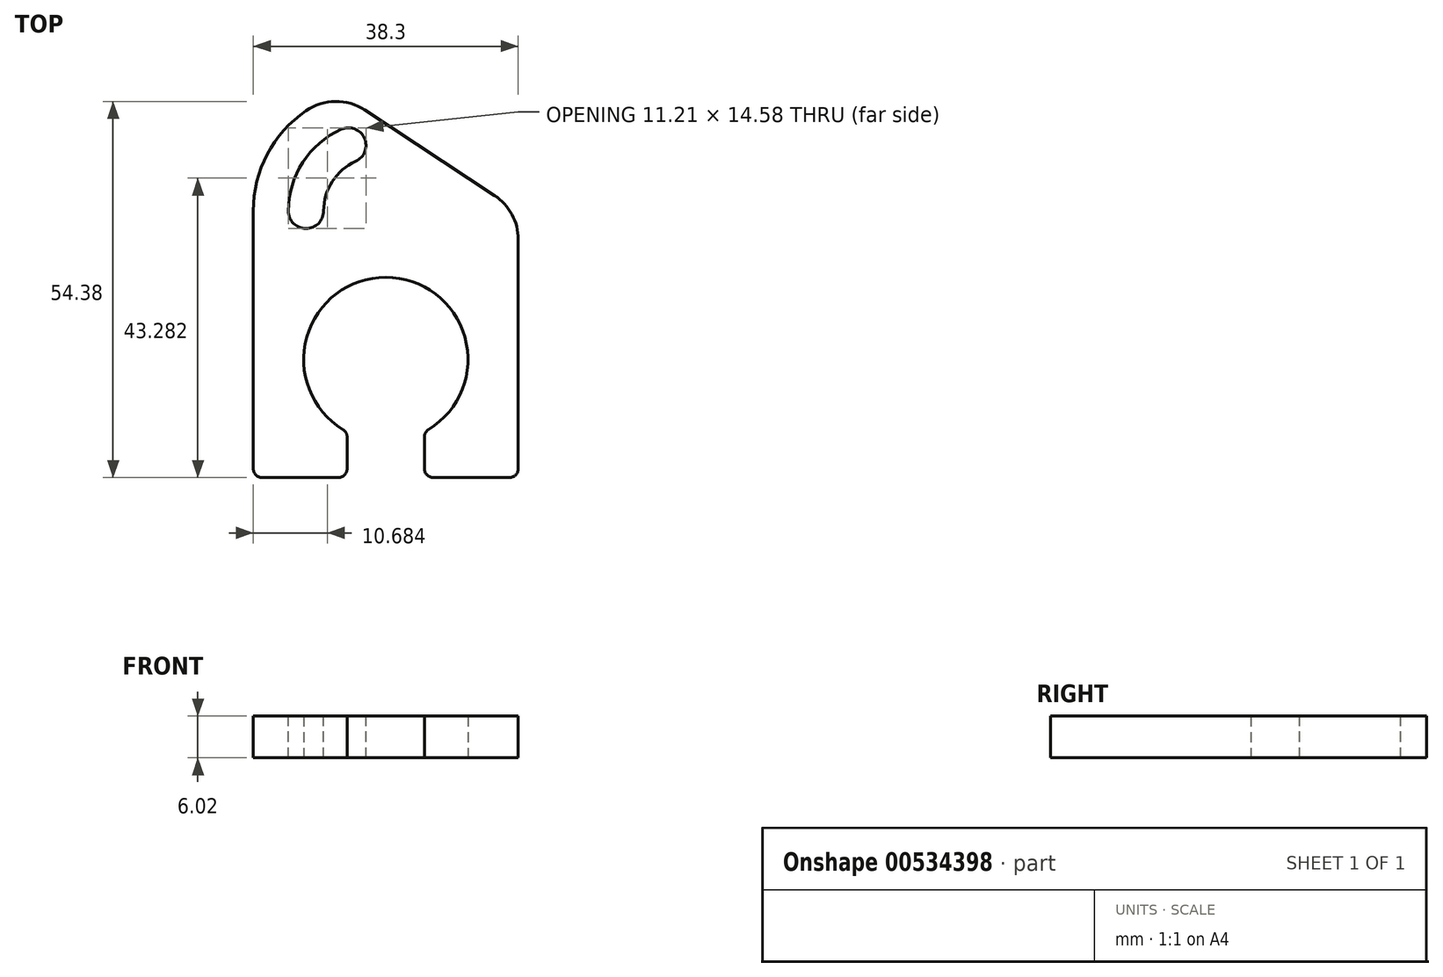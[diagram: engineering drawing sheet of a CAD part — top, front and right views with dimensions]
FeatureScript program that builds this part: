
annotation { "Feature Type Name" : "Feature", "Feature Type Description" : "" }
export const myFeature = defineFeature(function(context is Context, id is Id, definition is map)
    precondition{}
    {
        {
            var Q0;
            Q0=qCreatedBy(makeId("Top.planeOp"),FACE);
            var sketch = newSketch(context, id + "F0", { "sketchPlane" : qUnion([Q0])});
            skArc(sketch, "E0", {"start": v(5.59, -10.48) * mm, "mid": v(0, 11.87) * mm, "end": v(-5.59, -10.48) * mm});
            skLineSegment(sketch, "E1", {"start": v(19.15, -17.08) * mm, "end": v(19.15, 21.45) * mm});
            skLineSegment(sketch, "E2", {"start": v(19.15, 21.45) * mm, "end": v(-6.5, 38.34) * mm});
            skLineSegment(sketch, "E3", {"start": v(-19.15, -17.08) * mm, "end": v(-19.15, 21.45) * mm});
            skLineSegment(sketch, "E4", {"start": v(-19.15, -17.08) * mm, "end": v(-5.59, -17.08) * mm});
            skLineSegment(sketch, "E5", {"start": v(5.59, -17.08) * mm, "end": v(19.15, -17.08) * mm});
            skLineSegment(sketch, "E6", {"start": v(-5.59, -10.48) * mm, "end": v(-5.59, -17.08) * mm});
            skLineSegment(sketch, "E7", {"start": v(5.59, -10.48) * mm, "end": v(5.59, -17.08) * mm});
            skArc(sketch, "E8", {"start": v(-19.15, 21.45) * mm, "mid": v(-15.64, 32) * mm, "end": v(-6.5, 38.34) * mm});
            skSolve(sketch);
        }
        {
            var Q0;
            Q0=makeQuery(id+"F0.imprint","IMPRINT",FACE,{"disambiguationData":[TD([[makeQuery(id+"F0.imprint","IMPRINT",EDGE,{"derivedFrom":sQuery(id+"F0.wireOp",EDGE,"E0")}),-1.0]])]});
            extrude(context, id + "F1", {"entities" : qUnion([Q0]), "depth" : 6.02 * mm, "offsetDistance" : 25.4 * mm});
        }
        {
            var Q0;
            Q0=makeQuery(id+"F1.opExtrude","CAP_FACE",FACE,{"disambiguationData":[OSD([sQuery(id+"F0.wireOp",EDGE,"E0"),sQuery(id+"F0.wireOp",EDGE,"E1"),sQuery(id+"F0.wireOp",EDGE,"E2"),sQuery(id+"F0.wireOp",EDGE,"E3"),sQuery(id+"F0.wireOp",EDGE,"E4"),sQuery(id+"F0.wireOp",EDGE,"E5"),sQuery(id+"F0.wireOp",EDGE,"E6"),sQuery(id+"F0.wireOp",EDGE,"E7"),sQuery(id+"F0.wireOp",EDGE,"E8")])],"isStart":false});
            var sketch = newSketch(context, id + "F2", { "sketchPlane" : qUnion([Q0])});
            skArc(sketch, "E9", {"start": v(-14.07, 21.45) * mm, "mid": v(-11.53, 18.91) * mm, "end": v(-9, 21.45) * mm});
            skArc(sketch, "E10", {"start": v(-14.07, 21.45) * mm, "mid": v(-12, 28.48) * mm, "end": v(-6.44, 33.27) * mm});
            skArc(sketch, "E11", {"start": v(-9, 21.45) * mm, "mid": v(-7.73, 25.73) * mm, "end": v(-4.35, 28.64) * mm});
            skArc(sketch, "E12", {"start": v(-4.35, 28.64) * mm, "mid": v(-3.08, 32) * mm, "end": v(-6.44, 33.27) * mm});
            skSolve(sketch);
        }
        {
            var Q0;
            Q0=makeQuery(id+"F2.imprint","IMPRINT",FACE,{"disambiguationData":[TD([[makeQuery(id+"F2.imprint","IMPRINT",EDGE,{"derivedFrom":sQuery(id+"F2.wireOp",EDGE,"E9")}),1.0]])]});
            var Q1;
            Q1=makeQuery(id+"F1.opExtrude","CAP_FACE",FACE,{"disambiguationData":[OSD([sQuery(id+"F0.wireOp",EDGE,"E0"),sQuery(id+"F0.wireOp",EDGE,"E1"),sQuery(id+"F0.wireOp",EDGE,"E2"),sQuery(id+"F0.wireOp",EDGE,"E3"),sQuery(id+"F0.wireOp",EDGE,"E4"),sQuery(id+"F0.wireOp",EDGE,"E5"),sQuery(id+"F0.wireOp",EDGE,"E6"),sQuery(id+"F0.wireOp",EDGE,"E7"),sQuery(id+"F0.wireOp",EDGE,"E8")])],"isStart":true});
            extrude(context, id + "F3", {"entities" : qUnion([Q0]), "operationType" : NewBodyOperationType.REMOVE, "endBound" : BoundingType.UP_TO_SURFACE, "oppositeDirection" : true, "depth" : 25.4 * mm, "endBoundEntityFace" : qUnion([Q1]), "offsetDistance" : 25.4 * mm});
        }
        {
            var Q0;
            Q0=makeQuery(id+"F1.opExtrude","SWEPT_EDGE",EDGE,{"disambiguationData":[OSD([sQuery(id+"F0.wireOp",EDGE,"E2"),sQuery(id+"F0.wireOp",EDGE,"E8")])]});
            var Q1;
            Q1=makeQuery(id+"F1.opExtrude","SWEPT_EDGE",EDGE,{"disambiguationData":[OSD([sQuery(id+"F0.wireOp",EDGE,"E1"),sQuery(id+"F0.wireOp",EDGE,"E2")])]});
            fillet(context, id + "F4", {"entities" : qUnion([Q0, Q1]), "radius" : 7.62 * mm, "tangentPropagation" : true, "allowEdgeOverflow" : false});
        }
        {
            var Q0;
            Q0=makeQuery(id+"F1.opExtrude","SWEPT_EDGE",EDGE,{"disambiguationData":[OSD([sQuery(id+"F0.wireOp",EDGE,"E3"),sQuery(id+"F0.wireOp",EDGE,"E4")])]});
            var Q1;
            Q1=makeQuery(id+"F1.opExtrude","SWEPT_EDGE",EDGE,{"disambiguationData":[OSD([sQuery(id+"F0.wireOp",EDGE,"E4"),sQuery(id+"F0.wireOp",EDGE,"E6")])]});
            var Q2;
            Q2=makeQuery(id+"F1.opExtrude","SWEPT_EDGE",EDGE,{"disambiguationData":[OSD([sQuery(id+"F0.wireOp",EDGE,"E5"),sQuery(id+"F0.wireOp",EDGE,"E7")])]});
            var Q3;
            Q3=makeQuery(id+"F1.opExtrude","SWEPT_EDGE",EDGE,{"disambiguationData":[OSD([sQuery(id+"F0.wireOp",EDGE,"E1"),sQuery(id+"F0.wireOp",EDGE,"E5")])]});
            var Q4;
            Q4=makeQuery(id+"F1.opExtrude","SWEPT_EDGE",EDGE,{"disambiguationData":[OSD([sQuery(id+"F0.wireOp",EDGE,"E0"),sQuery(id+"F0.wireOp",EDGE,"E7")])]});
            var Q5;
            Q5=makeQuery(id+"F1.opExtrude","SWEPT_EDGE",EDGE,{"disambiguationData":[OSD([sQuery(id+"F0.wireOp",EDGE,"E0"),sQuery(id+"F0.wireOp",EDGE,"E6")])]});
            fillet(context, id + "F5", {"entities" : qUnion([Q0, Q1, Q2, Q3, Q4, Q5]), "radius" : 1.27 * mm, "tangentPropagation" : true, "allowEdgeOverflow" : false});
        }
    });
